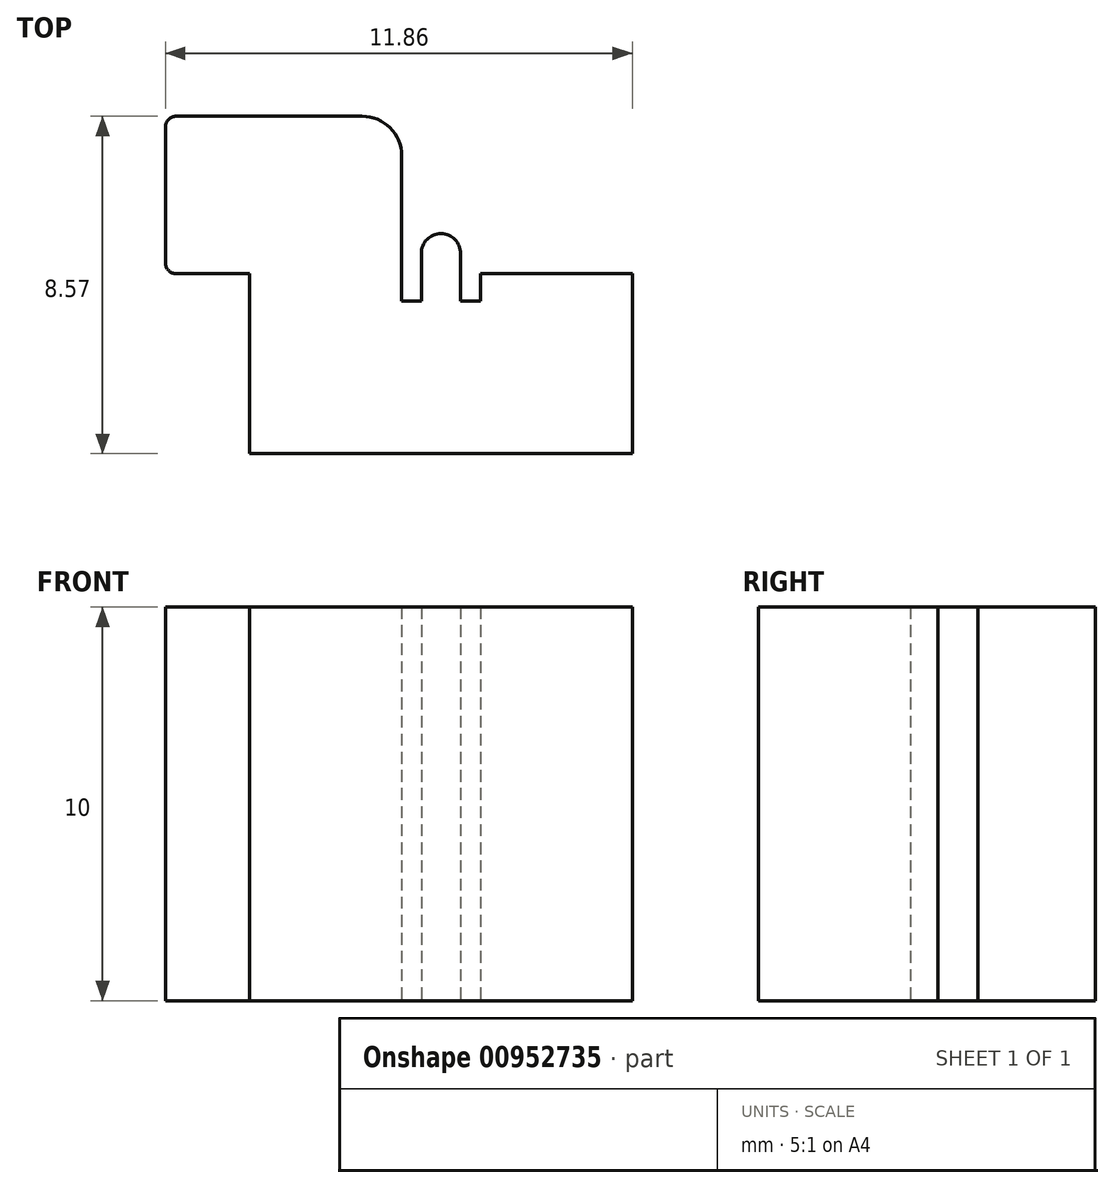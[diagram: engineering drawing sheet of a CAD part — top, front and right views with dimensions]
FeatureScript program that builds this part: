
annotation { "Feature Type Name" : "Feature", "Feature Type Description" : "" }
export const myFeature = defineFeature(function(context is Context, id is Id, definition is map)
    precondition{}
    {
        {
            var Q0;
            Q0=qCreatedBy(makeId("Top.planeOp"),FACE);
            var sketch = newSketch(context, id + "F0", { "sketchPlane" : qUnion([Q0])});
            skLineSegment(sketch, "E0.bottom", {"start": v(-1, -2) * mm, "end": v(-6.73, -2) * mm});
            skLineSegment(sketch, "E0.top", {"start": v(-2, 2) * mm, "end": v(-6.73, 2) * mm});
            skLineSegment(sketch, "E0.left", {"start": v(-1, -2) * mm, "end": v(-1, 1) * mm});
            skLineSegment(sketch, "E0.right", {"start": v(-7, -1.73) * mm, "end": v(-7, 1.73) * mm});
            skPoint(sketch, "E0.middle", {"position": v(-4, 0) * mm});
            skLineSegment(sketch, "E1", {"start": v(0, -13.39) * mm, "end": v(0, -5.13) * mm});
            skLineSegment(sketch, "E2.bottom", {"start": v(0.5, -6.57) * mm, "end": v(-0.5, -6.57) * mm});
            skLineSegment(sketch, "E2.top", {"start": v(0.5, -1.48) * mm, "end": v(-0.5, -1.48) * mm});
            skLineSegment(sketch, "E2.left", {"start": v(0.5, -6.57) * mm, "end": v(0.5, -1.48) * mm});
            skLineSegment(sketch, "E2.right", {"start": v(-0.5, -6.57) * mm, "end": v(-0.5, -1.48) * mm});
            skPoint(sketch, "E2.middle", {"position": v(0, -4.03) * mm});
            skCircle(sketch, "E3", {"center": v(0, -1.48) * mm, "radius": 0.5 * mm});
            skPoint(sketch, "E4.visualSharp", {"position": v(-1, 2) * mm});
            skArc(sketch, "E4.filletArc", {"start": v(-1, 1) * mm, "mid": v(-1.3, 1.7) * mm, "end": v(-2, 2) * mm});
            skLineSegment(sketch, "E5", {"start": v(-1, -2) * mm, "end": v(-1, -2.7) * mm});
            skLineSegment(sketch, "E6", {"start": v(-1, -2.7) * mm, "end": v(-0.5, -2.7) * mm});
            skLineSegment(sketch, "E7", {"start": v(-4.86, -2) * mm, "end": v(-4.86, -6.57) * mm});
            skLineSegment(sketch, "E8", {"start": v(-4.86, -6.57) * mm, "end": v(-0.5, -6.57) * mm});
            skPoint(sketch, "E9.visualSharp", {"position": v(-7, 2) * mm});
            skArc(sketch, "E9.filletArc", {"start": v(-6.73, 2) * mm, "mid": v(-6.92, 1.92) * mm, "end": v(-7, 1.73) * mm});
            skPoint(sketch, "E10.visualSharp", {"position": v(-7, -2) * mm});
            skArc(sketch, "E10.filletArc", {"start": v(-7, -1.73) * mm, "mid": v(-6.92, -1.92) * mm, "end": v(-6.73, -2) * mm});
            skLineSegment(sketch, "E11.MirrorCS", {"start": v(7, -1.73) * mm, "end": v(7, 1.73) * mm});
            skLineSegment(sketch, "E12.MirrorCS", {"start": v(2, 2) * mm, "end": v(6.73, 2) * mm});
            skArc(sketch, "E13.MirrorCS", {"start": v(6.73, 2) * mm, "mid": v(6.92, 1.92) * mm, "end": v(7, 1.73) * mm});
            skArc(sketch, "E14.MirrorCS", {"start": v(7, -1.73) * mm, "mid": v(6.92, -1.92) * mm, "end": v(6.73, -2) * mm});
            skPoint(sketch, "E15.MirrorP", {"position": v(1, 2) * mm});
            skPoint(sketch, "E16.MirrorP", {"position": v(4, 0) * mm});
            skLineSegment(sketch, "E17.MirrorCS", {"start": v(1, -2) * mm, "end": v(1, 1) * mm});
            skLineSegment(sketch, "E18.MirrorCS", {"start": v(1, -2) * mm, "end": v(6.73, -2) * mm});
            skPoint(sketch, "E19.MirrorP", {"position": v(7, 2) * mm});
            skArc(sketch, "E20.MirrorCS", {"start": v(1, 1) * mm, "mid": v(1.3, 1.7) * mm, "end": v(2, 2) * mm});
            skPoint(sketch, "E21.MirrorP", {"position": v(7, -2) * mm});
            skLineSegment(sketch, "E22.MirrorCS", {"start": v(1, -2) * mm, "end": v(1, -2.7) * mm});
            skLineSegment(sketch, "E23.MirrorCS", {"start": v(1, -2.7) * mm, "end": v(0.5, -2.7) * mm});
            skLineSegment(sketch, "E24.MirrorCS", {"start": v(4.86, -6.57) * mm, "end": v(0.5, -6.57) * mm});
            skLineSegment(sketch, "E25.MirrorCS", {"start": v(4.86, -2) * mm, "end": v(4.86, -6.57) * mm});
            skSolve(sketch);
        }
        {
            var Q0;
            Q0=makeQuery(id+"F0.imprint","IMPRINT",FACE,{"disambiguationData":[TD([[makeQuery(id+"F0.imprint","IMPRINT",EDGE,{"derivedFrom":sQuery(id+"F0.wireOp",EDGE,"E0.top")}),1.0]])]});
            var Q1;
            {var subQ1=sQuery(id+"F0.wireOp",EDGE,"E14.MirrorCS");Q1=makeQuery(id+"F0.imprint","IMPRINT",FACE,{"disambiguationData":[TD([[makeQuery(id+"F0.imprint","IMPRINT",EDGE,{"derivedFrom":subQ1}),-1.0]])]});}
            var Q2;
            {var subQ3=sQuery(id+"F0.wireOp",EDGE,"E22.MirrorCS");Q2=makeQuery(id+"F0.imprint","IMPRINT",FACE,{"disambiguationData":[TD([[makeQuery(id+"F0.imprint","IMPRINT",EDGE,{"derivedFrom":subQ3}),1.0]])]});}
            var Q3;
            {var subQ0=sQuery(id+"F0.wireOp",EDGE,"E5");Q3=makeQuery(id+"F0.imprint","IMPRINT",FACE,{"disambiguationData":[TD([[makeQuery(id+"F0.imprint","IMPRINT",EDGE,{"derivedFrom":subQ0}),-1.0]])]});}
            var Q4;
            {var subQ5=sQuery(id+"F0.wireOp",EDGE,"E2.left");var subQ8=makeQuery(id+"F0.imprint","INTERSECT",VERTEX,{"derivedFrom":[subQ5,sQuery(id+"F0.wireOp",EDGE,"E23.MirrorCS")]});Q4=makeQuery(id+"F0.imprint","IMPRINT",FACE,{"disambiguationData":[TD([[makeQuery(id+"F0.imprint","IMPRINT",EDGE,{"disambiguationData":[TD([[subQ8,1.0]])],"derivedFrom":subQ5}),1.0]])]});}
            var Q5;
            {var subQ0=sQuery(id+"F0.wireOp",EDGE,"E2.top");Q5=makeQuery(id+"F0.imprint","IMPRINT",FACE,{"disambiguationData":[TD([[makeQuery(id+"F0.imprint","IMPRINT",EDGE,{"derivedFrom":subQ0}),-1.0]])]});}
            var Q6;
            {var subQ0=sQuery(id+"F0.wireOp",EDGE,"E2.top");Q6=makeQuery(id+"F0.imprint","IMPRINT",FACE,{"disambiguationData":[TD([[makeQuery(id+"F0.imprint","IMPRINT",EDGE,{"derivedFrom":subQ0}),1.0]])]});}
            extrude(context, id + "F1", {"entities" : qUnion([Q0, Q1, Q2, Q3, Q4, Q5, Q6]), "depth" : 10 * mm, "offsetDistance" : 25 * mm});
        }
    });
